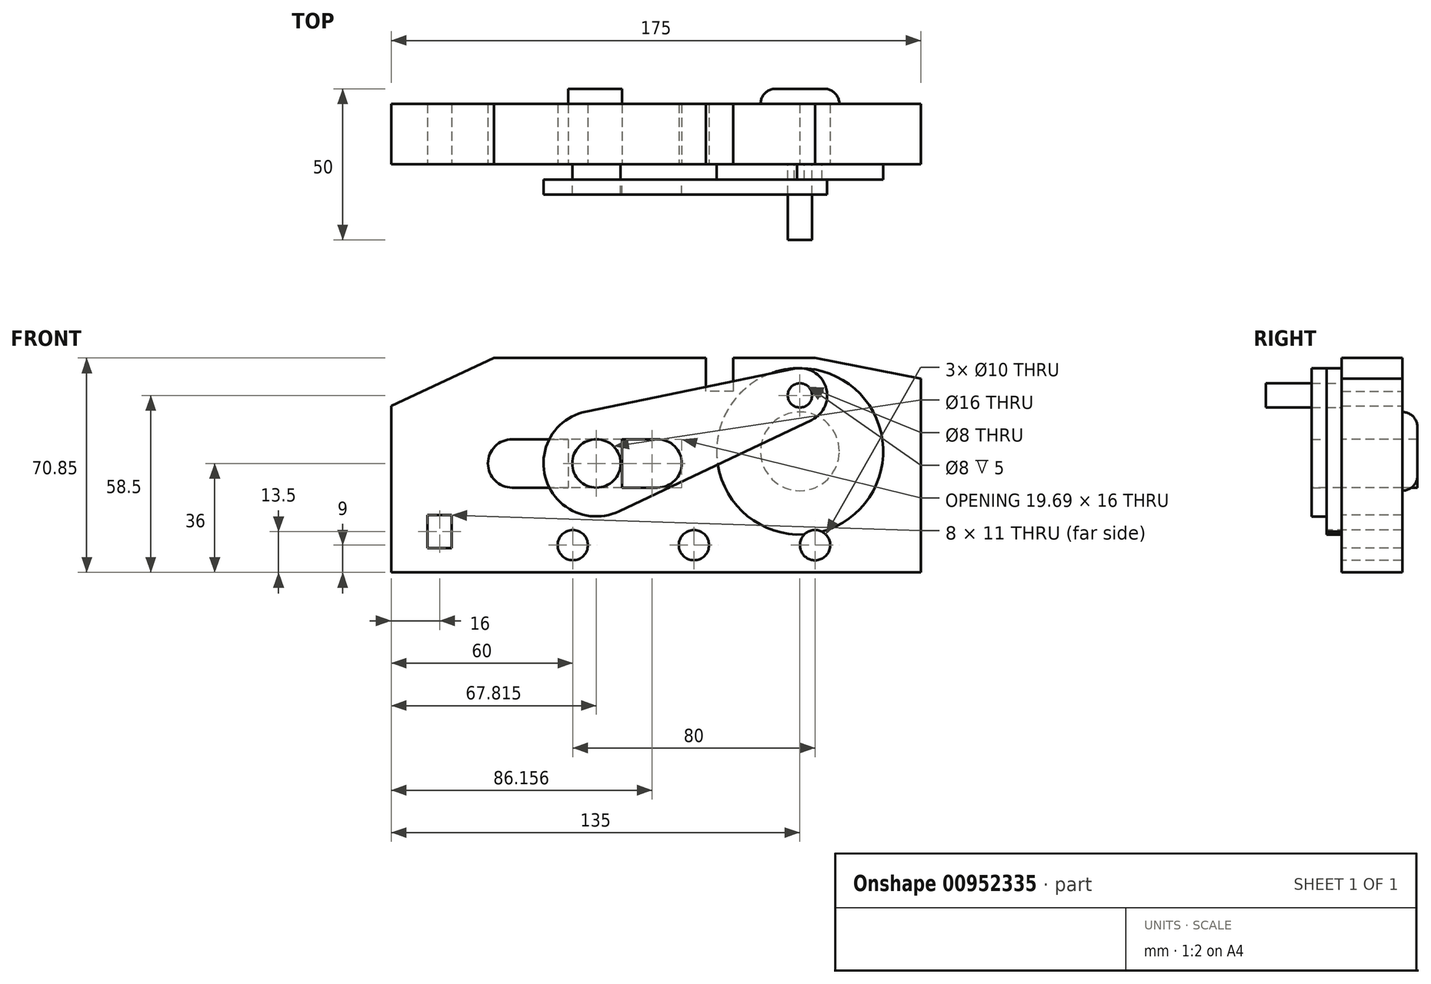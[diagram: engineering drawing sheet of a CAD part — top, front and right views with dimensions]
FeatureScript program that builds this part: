
annotation { "Feature Type Name" : "Feature", "Feature Type Description" : "" }
export const myFeature = defineFeature(function(context is Context, id is Id, definition is map)
    precondition{}
    {
        {
            var Q0;
            Q0=qCreatedBy(makeId("Front.planeOp"),FACE);
            var sketch = newSketch(context, id + "F0", { "sketchPlane" : qUnion([Q0])});
            skLineSegment(sketch, "E0", {"start": v(0, 0) * mm, "end": v(175, 0) * mm});
            skLineSegment(sketch, "E1", {"start": v(175, 0) * mm, "end": v(175, 64) * mm});
            skLineSegment(sketch, "E2", {"start": v(175, 64) * mm, "end": v(140, 70.85) * mm});
            skLineSegment(sketch, "E3", {"start": v(140, 70.85) * mm, "end": v(113, 70.85) * mm});
            skLineSegment(sketch, "E4", {"start": v(113, 70.85) * mm, "end": v(113, 59.85) * mm});
            skLineSegment(sketch, "E5", {"start": v(113, 59.85) * mm, "end": v(104, 59.85) * mm});
            skLineSegment(sketch, "E6", {"start": v(104, 59.85) * mm, "end": v(104, 70.85) * mm});
            skLineSegment(sketch, "E7", {"start": v(104, 70.85) * mm, "end": v(34, 70.85) * mm});
            skLineSegment(sketch, "E8", {"start": v(34, 70.85) * mm, "end": v(0, 55) * mm});
            skLineSegment(sketch, "E9", {"start": v(0, 55) * mm, "end": v(0, 0) * mm});
            skSolve(sketch);
        }
        {
            var Q0;
            Q0=makeQuery(id+"F0.imprint","IMPRINT",FACE,{"disambiguationData":[TD([[makeQuery(id+"F0.imprint","IMPRINT",EDGE,{"derivedFrom":sQuery(id+"F0.wireOp",EDGE,"E0")}),1.0]])]});
            extrude(context, id + "F1", {"entities" : qUnion([Q0]), "depth" : 20 * mm, "offsetDistance" : 25 * mm});
        }
        {
            var Q0;
            Q0=makeQuery(id+"F1.opExtrude","CAP_FACE",FACE,{"disambiguationData":[OSD([sQuery(id+"F0.wireOp",EDGE,"E0"),sQuery(id+"F0.wireOp",EDGE,"E1"),sQuery(id+"F0.wireOp",EDGE,"E2"),sQuery(id+"F0.wireOp",EDGE,"E3"),sQuery(id+"F0.wireOp",EDGE,"E4"),sQuery(id+"F0.wireOp",EDGE,"E5"),sQuery(id+"F0.wireOp",EDGE,"E6"),sQuery(id+"F0.wireOp",EDGE,"E7"),sQuery(id+"F0.wireOp",EDGE,"E8"),sQuery(id+"F0.wireOp",EDGE,"E9")])],"isStart":false});
            var sketch = newSketch(context, id + "F2", { "sketchPlane" : qUnion([Q0])});
            skCircle(sketch, "E10", {"center": v(60, 9) * mm, "radius": 5 * mm});
            skCircle(sketch, "E11", {"center": v(100, 9) * mm, "radius": 5 * mm});
            skCircle(sketch, "E12", {"center": v(140, 9) * mm, "radius": 5 * mm});
            skLineSegment(sketch, "E13.bottom", {"start": v(12, 8) * mm, "end": v(20, 8) * mm});
            skLineSegment(sketch, "E13.top", {"start": v(12, 19) * mm, "end": v(20, 19) * mm});
            skLineSegment(sketch, "E13.left", {"start": v(12, 8) * mm, "end": v(12, 19) * mm});
            skLineSegment(sketch, "E13.right", {"start": v(20, 8) * mm, "end": v(20, 19) * mm});
            skCircle(sketch, "E14", {"center": v(135, 40) * mm, "radius": 10 * mm});
            skArc(sketch, "E15", {"start": v(40, 44) * mm, "mid": v(32, 36) * mm, "end": v(40, 28) * mm});
            skArc(sketch, "E16", {"start": v(88, 28) * mm, "mid": v(96, 36) * mm, "end": v(88, 44) * mm});
            skLineSegment(sketch, "E17", {"start": v(40, 44) * mm, "end": v(88, 44) * mm});
            skLineSegment(sketch, "E18", {"start": v(40, 28) * mm, "end": v(88, 28) * mm});
            skSolve(sketch);
        }
        {
            var Q0;
            Q0=makeQuery(id+"F2.imprint","IMPRINT",FACE,{"disambiguationData":[TD([[makeQuery(id+"F2.imprint","IMPRINT",EDGE,{"derivedFrom":sQuery(id+"F2.wireOp",EDGE,"E13.bottom")}),1.0]])]});
            var Q1;
            Q1=makeQuery(id+"F2.imprint","IMPRINT",FACE,{"disambiguationData":[TD([[makeQuery(id+"F2.imprint","IMPRINT",EDGE,{"derivedFrom":sQuery(id+"F2.wireOp",EDGE,"E10")}),1.0]])]});
            var Q2;
            Q2=makeQuery(id+"F2.imprint","IMPRINT",FACE,{"disambiguationData":[TD([[makeQuery(id+"F2.imprint","IMPRINT",EDGE,{"derivedFrom":sQuery(id+"F2.wireOp",EDGE,"E15")}),1.0]])]});
            var Q3;
            Q3=makeQuery(id+"F2.imprint","IMPRINT",FACE,{"disambiguationData":[TD([[makeQuery(id+"F2.imprint","IMPRINT",EDGE,{"derivedFrom":sQuery(id+"F2.wireOp",EDGE,"E14")}),1.0]])]});
            var Q4;
            Q4=makeQuery(id+"F2.imprint","IMPRINT",FACE,{"disambiguationData":[TD([[makeQuery(id+"F2.imprint","IMPRINT",EDGE,{"derivedFrom":sQuery(id+"F2.wireOp",EDGE,"E11")}),1.0]])]});
            var Q5;
            Q5=makeQuery(id+"F2.imprint","IMPRINT",FACE,{"disambiguationData":[TD([[makeQuery(id+"F2.imprint","IMPRINT",EDGE,{"derivedFrom":sQuery(id+"F2.wireOp",EDGE,"E12")}),1.0]])]});
            var Q6;
            Q6=makeQuery(id+"F1.opExtrude","CAP_FACE",FACE,{"disambiguationData":[OSD([sQuery(id+"F0.wireOp",EDGE,"E0"),sQuery(id+"F0.wireOp",EDGE,"E1"),sQuery(id+"F0.wireOp",EDGE,"E2"),sQuery(id+"F0.wireOp",EDGE,"E3"),sQuery(id+"F0.wireOp",EDGE,"E4"),sQuery(id+"F0.wireOp",EDGE,"E5"),sQuery(id+"F0.wireOp",EDGE,"E6"),sQuery(id+"F0.wireOp",EDGE,"E7"),sQuery(id+"F0.wireOp",EDGE,"E8"),sQuery(id+"F0.wireOp",EDGE,"E9")])],"isStart":true});
            extrude(context, id + "F3", {"entities" : qUnion([Q0, Q1, Q2, Q3, Q4, Q5]), "operationType" : NewBodyOperationType.REMOVE, "endBound" : BoundingType.UP_TO_SURFACE, "oppositeDirection" : true, "depth" : 25 * mm, "endBoundEntityFace" : qUnion([Q6]), "offsetDistance" : 25 * mm});
        }
        {
            var Q0;
            Q0=makeQuery(id+"F1.opExtrude","CAP_FACE",FACE,{"disambiguationData":[OSD([sQuery(id+"F0.wireOp",EDGE,"E0"),sQuery(id+"F0.wireOp",EDGE,"E1"),sQuery(id+"F0.wireOp",EDGE,"E2"),sQuery(id+"F0.wireOp",EDGE,"E3"),sQuery(id+"F0.wireOp",EDGE,"E4"),sQuery(id+"F0.wireOp",EDGE,"E5"),sQuery(id+"F0.wireOp",EDGE,"E6"),sQuery(id+"F0.wireOp",EDGE,"E7"),sQuery(id+"F0.wireOp",EDGE,"E8"),sQuery(id+"F0.wireOp",EDGE,"E9")])],"isStart":false});
            var sketch = newSketch(context, id + "F4", { "sketchPlane" : qUnion([Q0])});
            skCircle(sketch, "E19", {"center": v(135, 40) * mm, "radius": 27.5 * mm});
            skCircle(sketch, "E20", {"center": v(135, 58.5) * mm, "radius": 4 * mm});
            skLineSegment(sketch, "E21", {"start": v(135, 40) * mm, "end": v(135, 58.5) * mm});
            skLineSegment(sketch, "E22.0", {"start": v(40, 28) * mm, "end": v(88, 28) * mm, "construction": true});
            skLineSegment(sketch, "E23.0", {"start": v(40, 44) * mm, "end": v(88, 44) * mm, "construction": true});
            skCircle(sketch, "E24", {"center": v(67.81, 36) * mm, "radius": 8 * mm});
            skLineSegment(sketch, "E25", {"start": v(67.81, 36) * mm, "end": v(135, 58.5) * mm, "construction": true});
            skArc(sketch, "E26", {"start": v(138.86, 50.37) * mm, "mid": v(143.53, 61.36) * mm, "end": v(133.19, 67.32) * mm});
            skLineSegment(sketch, "E27", {"start": v(64.29, 53.14) * mm, "end": v(134, 67.48) * mm});
            skLineSegment(sketch, "E28", {"start": v(75.32, 20.2) * mm, "end": v(138.86, 50.37) * mm});
            skArc(sketch, "E29.trimOffspring", {"start": v(64.29, 53.14) * mm, "mid": v(51.22, 30.44) * mm, "end": v(75.32, 20.2) * mm});
            skCircle(sketch, "E30", {"center": v(135, 40) * mm, "radius": 13 * mm});
            skLineSegment(sketch, "E31.bottom", {"start": v(58.54, 44) * mm, "end": v(76.31, 44) * mm});
            skLineSegment(sketch, "E31.top", {"start": v(58.54, 28) * mm, "end": v(76.31, 28) * mm});
            skLineSegment(sketch, "E31.left", {"start": v(58.54, 44) * mm, "end": v(58.54, 28) * mm});
            skLineSegment(sketch, "E31.right", {"start": v(76.31, 44) * mm, "end": v(76.31, 28) * mm});
            skSolve(sketch);
        }
        {
            var Q0;
            {var subQ1=sQuery(id+"F4.wireOp",EDGE,"E26");var subQ3=sQuery(id+"F4.wireOp",EDGE,"E28");var subQ5=makeQuery(id+"F4.imprint","INTERSECT",VERTEX,{"derivedFrom":[subQ1,subQ3]});Q0=makeQuery(id+"F4.imprint","IMPRINT",FACE,{"disambiguationData":[TD([[makeQuery(id+"F4.imprint","IMPRINT",EDGE,{"disambiguationData":[TD([[subQ5,-1.0]])],"derivedFrom":subQ1}),-1.0]])]});}
            var Q1;
            {var subQ5=sQuery(id+"F4.wireOp",EDGE,"E30");var subQ7=sQuery(id+"F4.wireOp",EDGE,"E21");var subQ8=makeQuery(id+"F4.imprint","INTERSECT",VERTEX,{"derivedFrom":[subQ7,subQ5]});Q1=makeQuery(id+"F4.imprint","IMPRINT",FACE,{"disambiguationData":[TD([[makeQuery(id+"F4.imprint","IMPRINT",EDGE,{"disambiguationData":[TD([[subQ8,1.0]])],"derivedFrom":subQ7}),-1.0]])]});}
            var Q2;
            {var subQ0=sQuery(id+"F4.wireOp",EDGE,"E30");var subQ1=sQuery(id+"F4.wireOp",EDGE,"E21");var subQ2=makeQuery(id+"F4.imprint","INTERSECT",VERTEX,{"derivedFrom":[subQ1,subQ0]});Q2=makeQuery(id+"F4.imprint","IMPRINT",FACE,{"disambiguationData":[TD([[makeQuery(id+"F4.imprint","IMPRINT",EDGE,{"disambiguationData":[TD([[subQ2,1.0]])],"derivedFrom":subQ1}),1.0]])]});}
            var Q3;
            {var subQ0=sQuery(id+"F4.wireOp",EDGE,"E28");var subQ1=sQuery(id+"F4.wireOp",EDGE,"E21");var subQ2=makeQuery(id+"F4.imprint","INTERSECT",VERTEX,{"derivedFrom":[subQ1,subQ0]});Q3=makeQuery(id+"F4.imprint","IMPRINT",FACE,{"disambiguationData":[TD([[makeQuery(id+"F4.imprint","IMPRINT",EDGE,{"disambiguationData":[TD([[subQ2,-1.0]])],"derivedFrom":subQ1}),1.0]])]});}
            var Q4;
            {var subQ0=sQuery(id+"F4.wireOp",EDGE,"E28");var subQ1=makeQuery(id+"F4.imprint","INTERSECT",VERTEX,{"derivedFrom":[sQuery(id+"F4.wireOp",EDGE,"E21"),subQ0]});Q4=makeQuery(id+"F4.imprint","IMPRINT",FACE,{"disambiguationData":[TD([[makeQuery(id+"F4.imprint","IMPRINT",EDGE,{"disambiguationData":[TD([[subQ1,1.0]])],"derivedFrom":subQ0}),-1.0]])]});}
            var Q5;
            {var subQ0=sQuery(id+"F4.wireOp",EDGE,"E28");var subQ1=sQuery(id+"F4.wireOp",EDGE,"E21");var subQ2=makeQuery(id+"F4.imprint","INTERSECT",VERTEX,{"derivedFrom":[subQ1,subQ0]});Q5=makeQuery(id+"F4.imprint","IMPRINT",FACE,{"disambiguationData":[TD([[makeQuery(id+"F4.imprint","IMPRINT",EDGE,{"disambiguationData":[TD([[subQ2,-1.0]])],"derivedFrom":subQ1}),-1.0]])]});}
            extrude(context, id + "F5", {"entities" : qUnion([Q0, Q1, Q2, Q3, Q4, Q5]), "depth" : 5 * mm, "offsetDistance" : 25 * mm, "hasSecondDirection" : true, "secondDirectionOppositeDirection" : true, "secondDirectionDepth" : 25 * mm});
        }
        {
            var Q0;
            Q0=makeQuery(id+"F1.opExtrude","SWEPT_BODY",BODY,{"disambiguationData":[OSD([sQuery(id+"F0.wireOp",EDGE,"E0"),sQuery(id+"F0.wireOp",EDGE,"E1"),sQuery(id+"F0.wireOp",EDGE,"E2"),sQuery(id+"F0.wireOp",EDGE,"E3"),sQuery(id+"F0.wireOp",EDGE,"E4"),sQuery(id+"F0.wireOp",EDGE,"E5"),sQuery(id+"F0.wireOp",EDGE,"E6"),sQuery(id+"F0.wireOp",EDGE,"E7"),sQuery(id+"F0.wireOp",EDGE,"E8"),sQuery(id+"F0.wireOp",EDGE,"E9")])]});
            var Q1;
            Q1=makeQuery(id+"F5.opExtrude","SWEPT_BODY",BODY,{"disambiguationData":[OSD([sQuery(id+"F4.wireOp",EDGE,"E30")])]});
            booleanBodies(context, id + "F6", {"operationType" : BooleanOperationType.SUBTRACTION, "tools" : qUnion([Q0]), "targets" : qUnion([Q1]), "keepTools" : true});
        }
        {
            var Q0;
            Q0=makeQuery(id+"F5.opExtrude","CAP_EDGE",EDGE,{"disambiguationData":[OSD([sQuery(id+"F4.wireOp",EDGE,"E30")])],"isStart":true});
            fillet(context, id + "F7", {"entities" : qUnion([Q0]), "radius" : 5 * mm, "tangentPropagation" : true, "allowEdgeOverflow" : false});
        }
        {
            var Q0;
            {var subQ1=sQuery(id+"F4.wireOp",EDGE,"E19");var subQ5=sQuery(id+"F4.wireOp",EDGE,"E28");var subQ6=makeQuery(id+"F4.imprint","INTERSECT",VERTEX,{"derivedFrom":[subQ1,subQ5]});Q0=makeQuery(id+"F4.imprint","IMPRINT",FACE,{"disambiguationData":[TD([[makeQuery(id+"F4.imprint","IMPRINT",EDGE,{"disambiguationData":[TD([[subQ6,-1.0]])],"derivedFrom":subQ1}),1.0]])]});}
            var Q1;
            Q1=makeQuery(id+"F4.imprint","IMPRINT",FACE,{"disambiguationData":[TD([[makeQuery(id+"F4.imprint","IMPRINT",EDGE,{"derivedFrom":sQuery(id+"F4.wireOp",EDGE,"E20")}),-1.0]])]});
            var Q2;
            {var subQ0=sQuery(id+"F4.wireOp",EDGE,"E27");var subQ1=sQuery(id+"F4.wireOp",EDGE,"E19");var subQ2=makeQuery(id+"F4.imprint","INTERSECT",VERTEX,{"disambiguationData":[OD(0.0)],"derivedFrom":[subQ1,subQ0]});Q2=makeQuery(id+"F4.imprint","IMPRINT",FACE,{"disambiguationData":[TD([[makeQuery(id+"F4.imprint","IMPRINT",EDGE,{"disambiguationData":[TD([[subQ2,-1.0]])],"derivedFrom":subQ1}),1.0]])]});}
            var Q3;
            {var subQ0=sQuery(id+"F4.wireOp",EDGE,"E27");var subQ1=sQuery(id+"F4.wireOp",EDGE,"E19");var subQ2=makeQuery(id+"F4.imprint","INTERSECT",VERTEX,{"disambiguationData":[OD(0.0)],"derivedFrom":[subQ1,subQ0]});Q3=makeQuery(id+"F4.imprint","IMPRINT",FACE,{"disambiguationData":[TD([[makeQuery(id+"F4.imprint","IMPRINT",EDGE,{"disambiguationData":[TD([[subQ2,1.0]])],"derivedFrom":subQ1}),1.0]])]});}
            var Q4;
            {var subQ0=sQuery(id+"F4.wireOp",EDGE,"E19");var subQ1=makeQuery(id+"F3.boolean.opBoolean","COPY",EDGE,{"derivedFrom":makeQuery(id+"F3.opExtrude","CAP_EDGE",EDGE,{"disambiguationData":[OSD([sQuery(id+"F2.wireOp",EDGE,"E12")])],"isStart":true})});var subQ2=makeQuery(id+"F4.imprint","INTERSECT",VERTEX,{"disambiguationData":[OD(0.0)],"derivedFrom":[subQ1,subQ0]});Q4=makeQuery(id+"F4.imprint","IMPRINT",FACE,{"disambiguationData":[TD([[makeQuery(id+"F4.imprint","IMPRINT",EDGE,{"disambiguationData":[TD([[subQ2,-1.0]])],"derivedFrom":subQ0}),1.0]])]});}
            extrude(context, id + "F8", {"entities" : qUnion([Q0, Q1, Q2, Q3, Q4]), "operationType" : NewBodyOperationType.ADD, "depth" : 5 * mm, "offsetDistance" : 25 * mm});
        }
        {
            var Q0;
            Q0=makeQuery(id+"F4.imprint","IMPRINT",FACE,{"disambiguationData":[TD([[makeQuery(id+"F4.imprint","IMPRINT",EDGE,{"derivedFrom":sQuery(id+"F4.wireOp",EDGE,"E20")}),1.0]])]});
            extrude(context, id + "F9", {"entities" : qUnion([Q0]), "depth" : 25 * mm, "offsetDistance" : 25 * mm});
        }
        {
            var Q0;
            {var subQ1=makeQuery(id+"F1.opExtrude","CAP_EDGE",EDGE,{"disambiguationData":[OSD([sQuery(id+"F0.wireOp",EDGE,"E5")])],"isStart":false});Q0=makeQuery(id+"F4.imprint","IMPRINT",FACE,{"disambiguationData":[TD([[makeQuery(id+"F4.imprint","IMPRINT",EDGE,{"derivedFrom":subQ1}),1.0]])]});}
            var Q1;
            Q1=makeQuery(id+"F4.imprint","IMPRINT",FACE,{"disambiguationData":[TD([[makeQuery(id+"F4.imprint","IMPRINT",EDGE,{"derivedFrom":sQuery(id+"F4.wireOp",EDGE,"E20")}),-1.0]])]});
            var Q2;
            {var subQ0=sQuery(id+"F4.wireOp",EDGE,"E28");var subQ1=sQuery(id+"F4.wireOp",EDGE,"E21");var subQ2=makeQuery(id+"F4.imprint","INTERSECT",VERTEX,{"derivedFrom":[subQ1,subQ0]});Q2=makeQuery(id+"F4.imprint","IMPRINT",FACE,{"disambiguationData":[TD([[makeQuery(id+"F4.imprint","IMPRINT",EDGE,{"disambiguationData":[TD([[subQ2,-1.0]])],"derivedFrom":subQ1}),1.0]])]});}
            var Q3;
            {var subQ0=sQuery(id+"F4.wireOp",EDGE,"E30");var subQ1=sQuery(id+"F4.wireOp",EDGE,"E21");var subQ2=makeQuery(id+"F4.imprint","INTERSECT",VERTEX,{"derivedFrom":[subQ1,subQ0]});Q3=makeQuery(id+"F4.imprint","IMPRINT",FACE,{"disambiguationData":[TD([[makeQuery(id+"F4.imprint","IMPRINT",EDGE,{"disambiguationData":[TD([[subQ2,1.0]])],"derivedFrom":subQ1}),1.0]])]});}
            var Q4;
            {var subQ5=sQuery(id+"F4.wireOp",EDGE,"E30");var subQ7=sQuery(id+"F4.wireOp",EDGE,"E21");var subQ8=makeQuery(id+"F4.imprint","INTERSECT",VERTEX,{"derivedFrom":[subQ7,subQ5]});Q4=makeQuery(id+"F4.imprint","IMPRINT",FACE,{"disambiguationData":[TD([[makeQuery(id+"F4.imprint","IMPRINT",EDGE,{"disambiguationData":[TD([[subQ8,1.0]])],"derivedFrom":subQ7}),-1.0]])]});}
            var Q5;
            {var subQ0=sQuery(id+"F4.wireOp",EDGE,"E28");var subQ1=sQuery(id+"F4.wireOp",EDGE,"E21");var subQ2=makeQuery(id+"F4.imprint","INTERSECT",VERTEX,{"derivedFrom":[subQ1,subQ0]});Q5=makeQuery(id+"F4.imprint","IMPRINT",FACE,{"disambiguationData":[TD([[makeQuery(id+"F4.imprint","IMPRINT",EDGE,{"disambiguationData":[TD([[subQ2,-1.0]])],"derivedFrom":subQ1}),-1.0]])]});}
            var Q6;
            {var subQ5=makeQuery(id+"F1.opExtrude","CAP_EDGE",EDGE,{"disambiguationData":[OSD([sQuery(id+"F0.wireOp",EDGE,"E5")])],"isStart":false});Q6=makeQuery(id+"F4.imprint","IMPRINT",FACE,{"disambiguationData":[TD([[makeQuery(id+"F4.imprint","IMPRINT",EDGE,{"derivedFrom":subQ5}),-1.0]])]});}
            var Q7;
            {var subQ5=makeQuery(id+"F3.boolean.opBoolean","COPY",EDGE,{"derivedFrom":makeQuery(id+"F3.opExtrude","CAP_EDGE",EDGE,{"disambiguationData":[OSD([sQuery(id+"F2.wireOp",EDGE,"E16")])],"isStart":true})});Q7=makeQuery(id+"F4.imprint","IMPRINT",FACE,{"disambiguationData":[TD([[makeQuery(id+"F4.imprint","IMPRINT",EDGE,{"derivedFrom":subQ5}),1.0]])]});}
            var Q8;
            {var subQ0=sQuery(id+"F4.wireOp",EDGE,"E24");var subQ1=makeQuery(id+"F3.boolean.opBoolean","COPY",EDGE,{"derivedFrom":makeQuery(id+"F3.opExtrude","CAP_EDGE",EDGE,{"disambiguationData":[OSD([sQuery(id+"F2.wireOp",EDGE,"E17")])],"isStart":true})});var subQ2=makeQuery(id+"F4.imprint","INTERSECT",VERTEX,{"derivedFrom":[subQ1,subQ0]});Q8=makeQuery(id+"F4.imprint","IMPRINT",FACE,{"disambiguationData":[TD([[makeQuery(id+"F4.imprint","IMPRINT",EDGE,{"disambiguationData":[TD([[subQ2,-1.0]])],"derivedFrom":subQ0}),-1.0]])]});}
            var Q9;
            {var subQ5=sQuery(id+"F4.wireOp",EDGE,"E31.left");Q9=makeQuery(id+"F4.imprint","IMPRINT",FACE,{"disambiguationData":[TD([[makeQuery(id+"F4.imprint","IMPRINT",EDGE,{"derivedFrom":subQ5}),-1.0]])]});}
            extrude(context, id + "F10", {"entities" : qUnion([Q0, Q1, Q2, Q3, Q4, Q5, Q6, Q7, Q8, Q9]), "depth" : 10 * mm, "offsetDistance" : 25 * mm, "hasSecondDirection" : true, "secondDirectionOppositeDirection" : false, "secondDirectionDepth" : 5 * mm});
        }
        {
            var Q0;
            {var subQ0=sQuery(id+"F4.wireOp",EDGE,"E24");var subQ1=makeQuery(id+"F4.imprint","INTERSECT",VERTEX,{"derivedFrom":[makeQuery(id+"F3.boolean.opBoolean","COPY",EDGE,{"derivedFrom":makeQuery(id+"F3.opExtrude","CAP_EDGE",EDGE,{"disambiguationData":[OSD([sQuery(id+"F2.wireOp",EDGE,"E17")])],"isStart":true})}),subQ0]});Q0=makeQuery(id+"F4.imprint","IMPRINT",FACE,{"disambiguationData":[TD([[makeQuery(id+"F4.imprint","IMPRINT",EDGE,{"disambiguationData":[TD([[subQ1,-1.0]])],"derivedFrom":subQ0}),1.0]])]});}
            extrude(context, id + "F11", {"entities" : qUnion([Q0]), "oppositeDirection" : true, "depth" : 25 * mm, "offsetDistance" : 25 * mm, "hasSecondDirection" : true, "secondDirectionOppositeDirection" : false, "secondDirectionDepth" : 10 * mm});
        }
        {
            var Q0;
            {var subQ5=sQuery(id+"F4.wireOp",EDGE,"E31.left");Q0=makeQuery(id+"F4.imprint","IMPRINT",FACE,{"disambiguationData":[TD([[makeQuery(id+"F4.imprint","IMPRINT",EDGE,{"derivedFrom":subQ5}),1.0]])]});}
            var Q1;
            {var subQ5=sQuery(id+"F4.wireOp",EDGE,"E31.right");Q1=makeQuery(id+"F4.imprint","IMPRINT",FACE,{"disambiguationData":[TD([[makeQuery(id+"F4.imprint","IMPRINT",EDGE,{"derivedFrom":subQ5}),-1.0]])]});}
            extrude(context, id + "F12", {"entities" : qUnion([Q0, Q1]), "operationType" : NewBodyOperationType.ADD, "oppositeDirection" : true, "depth" : 25 * mm, "offsetDistance" : 25 * mm});
        }
    });
